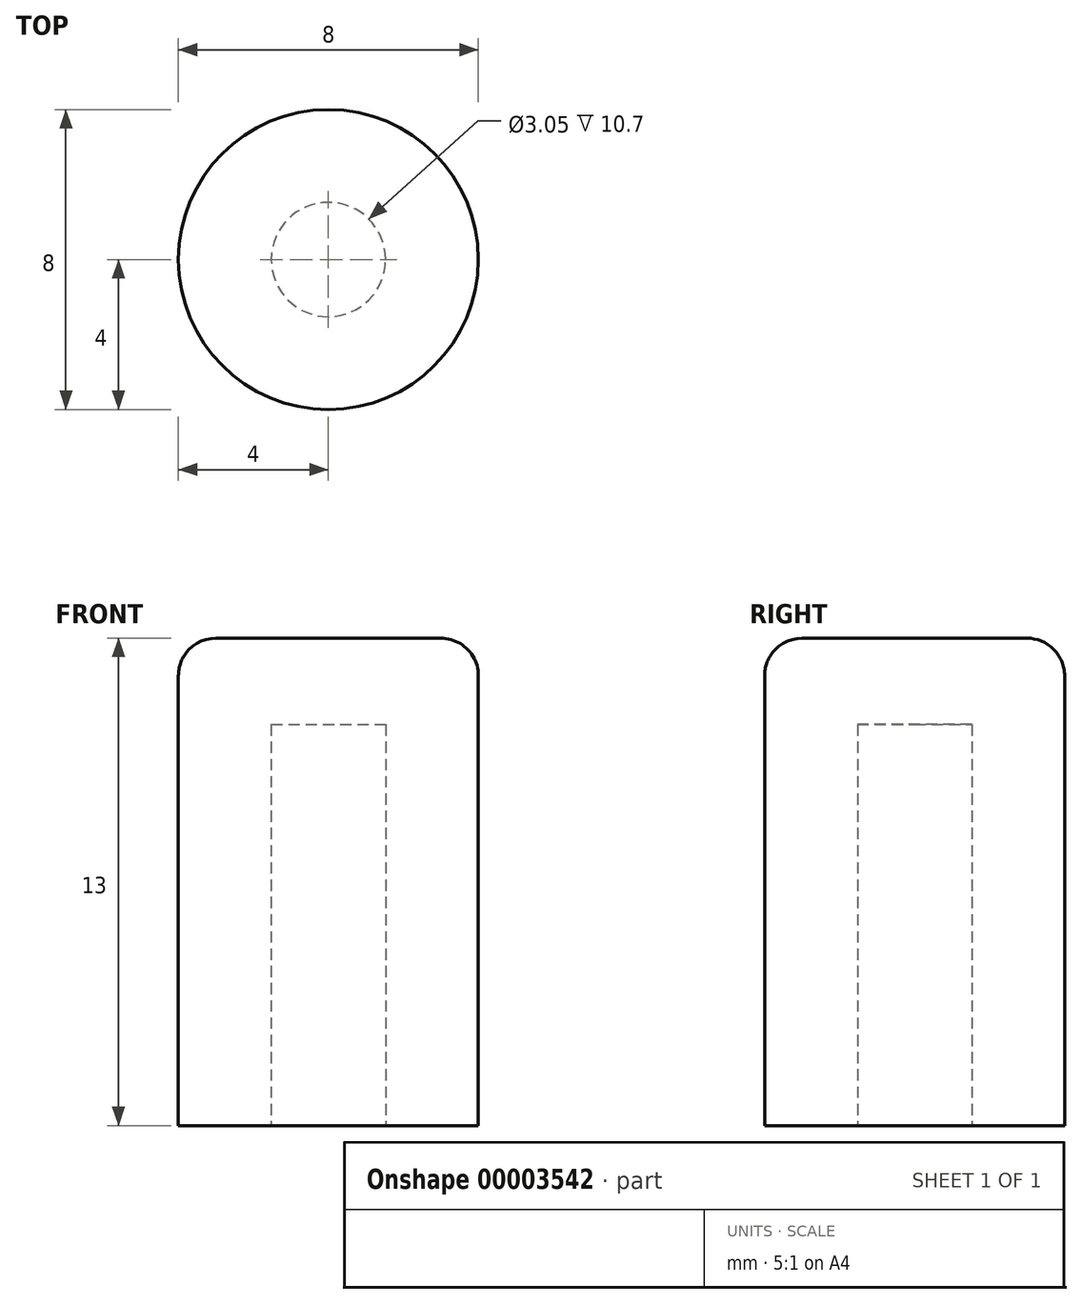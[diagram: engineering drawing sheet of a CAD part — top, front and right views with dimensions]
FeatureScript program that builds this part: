
annotation { "Feature Type Name" : "Feature", "Feature Type Description" : "" }
export const myFeature = defineFeature(function(context is Context, id is Id, definition is map)
    precondition{}
    {
        {
            var Q0;
            Q0=qCreatedBy(makeId("Top.planeOp"),FACE);
            var sketch = newSketch(context, id + "F0", { "sketchPlane" : qUnion([Q0])});
            skCircle(sketch, "E0", {"center": v(0, 0) * mm, "radius": 4 * mm});
            skSolve(sketch);
        }
        {
            var Q0;
            Q0 = qSketchRegion(id + "F0", true);
            extrude(context, id + "F1", {"entities" : qUnion([Q0]), "depth" : 13 * mm});
        }
        {
            var Q0;
            Q0=makeQuery(id+"F1.opExtrude","CAP_EDGE",EDGE,{"disambiguationData":[OSD([sQuery(id+"F0.wireOp",EDGE,"E0")])],"isStart":false});
            fillet(context, id + "F2", {"entities" : qUnion([Q0]), "radius" : 1 * mm, "tangentPropagation" : true, "allowEdgeOverflow" : false});
        }
        {
            var Q0;
            Q0=makeQuery(id+"F1.opExtrude","CAP_FACE",FACE,{"disambiguationData":[OSD([sQuery(id+"F0.wireOp",EDGE,"E0")])],"isStart":true});
            var sketch = newSketch(context, id + "F3", { "sketchPlane" : qUnion([Q0])});
            skCircle(sketch, "E1", {"center": v(0, 0) * mm, "radius": 1.52 * mm});
            skSolve(sketch);
        }
        {
            var Q0;
            Q0 = qSketchRegion(id + "F3", true);
            extrude(context, id + "F4", {"entities" : qUnion([Q0]), "operationType" : NewBodyOperationType.REMOVE, "oppositeDirection" : true, "depth" : 10.7 * mm});
        }
    });
